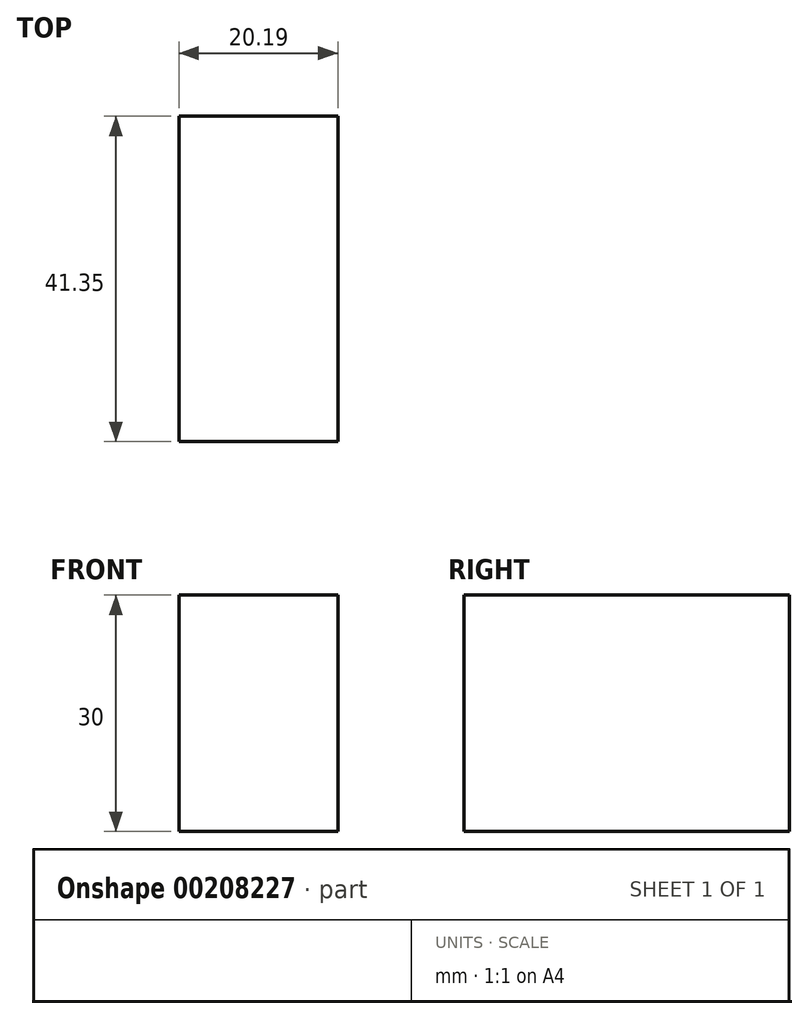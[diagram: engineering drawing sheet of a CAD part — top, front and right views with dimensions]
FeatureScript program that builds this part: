
annotation { "Feature Type Name" : "Feature", "Feature Type Description" : "" }
export const myFeature = defineFeature(function(context is Context, id is Id, definition is map)
    precondition{}
    {
        {
            var Q0;
            Q0=qCreatedBy(makeId("Top.planeOp"),FACE);
            var sketch = newSketch(context, id + "F0", { "sketchPlane" : qUnion([Q0])});
            skLineSegment(sketch, "E0.bottom", {"start": v(-64.5, 0) * mm, "end": v(-44.3, 0) * mm});
            skLineSegment(sketch, "E0.top", {"start": v(-64.5, -41.35) * mm, "end": v(-44.3, -41.35) * mm});
            skLineSegment(sketch, "E0.left", {"start": v(-64.5, 0) * mm, "end": v(-64.5, -41.35) * mm});
            skLineSegment(sketch, "E0.right", {"start": v(-44.3, 0) * mm, "end": v(-44.3, -41.35) * mm});
            skSolve(sketch);
        }
        {
            var Q0;
            Q0 = qSketchRegion(id + "F0", true);
            extrude(context, id + "F1", {"entities" : qUnion([Q0]), "depth" : 30 * mm});
        }
    });
